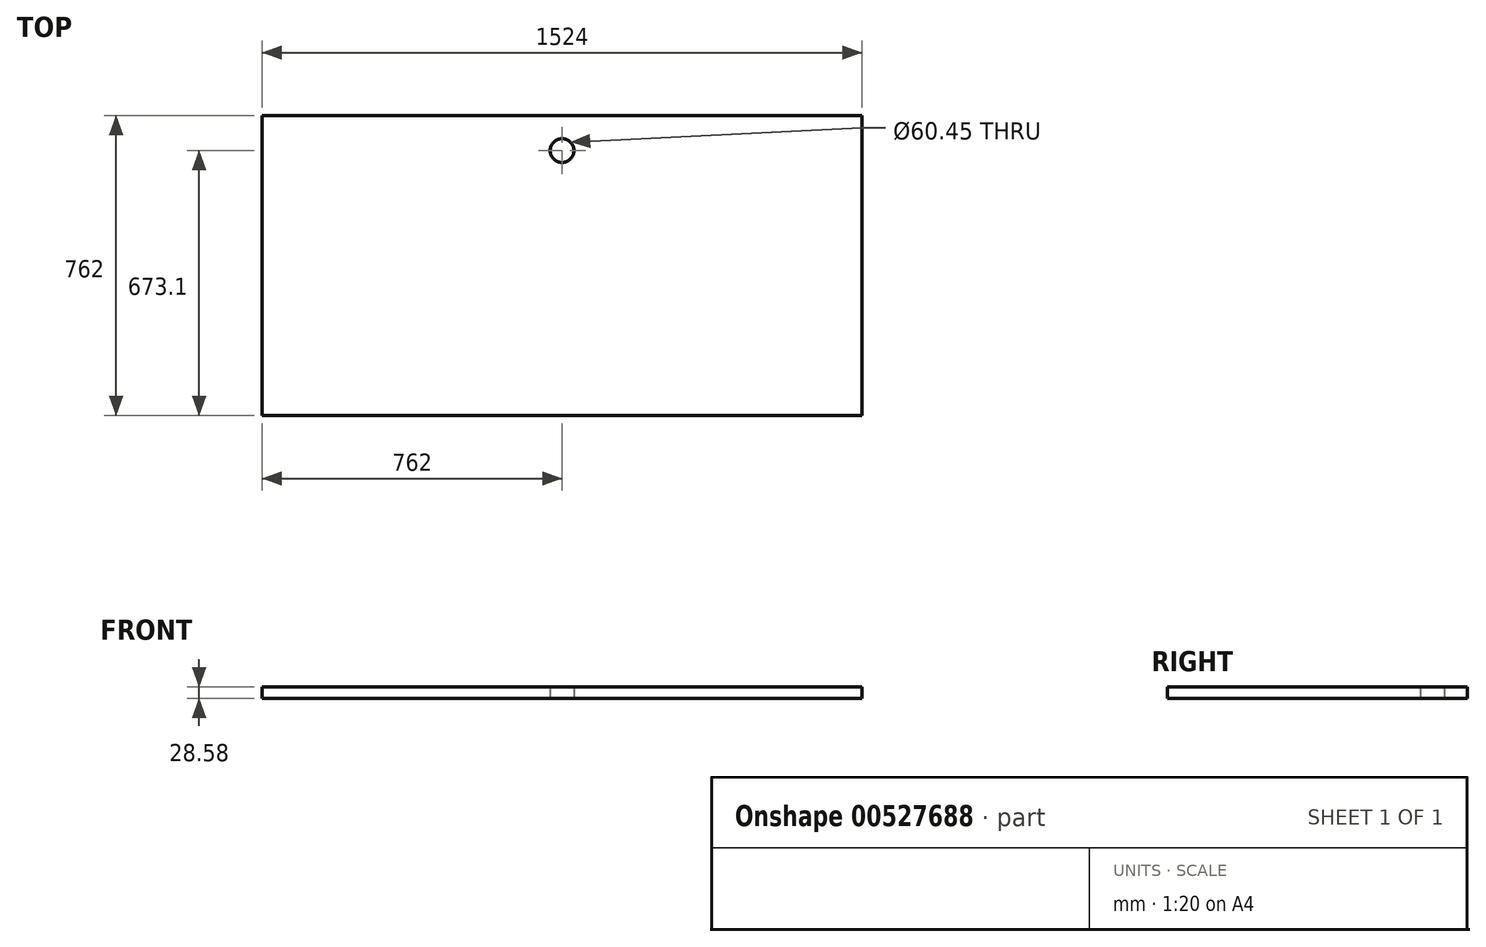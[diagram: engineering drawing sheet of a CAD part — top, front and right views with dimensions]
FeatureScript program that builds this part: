
annotation { "Feature Type Name" : "Feature", "Feature Type Description" : "" }
export const myFeature = defineFeature(function(context is Context, id is Id, definition is map)
    precondition{}
    {
        {
            var Q0;
            Q0=qCreatedBy(makeId("Top.planeOp"),FACE);
            var sketch = newSketch(context, id + "F0", { "sketchPlane" : qUnion([Q0])});
            skLineSegment(sketch, "E0.bottom", {"start": v(762, 381) * mm, "end": v(-762, 381) * mm});
            skLineSegment(sketch, "E0.top", {"start": v(762, -381) * mm, "end": v(-762, -381) * mm});
            skLineSegment(sketch, "E0.left", {"start": v(762, 381) * mm, "end": v(762, -381) * mm});
            skLineSegment(sketch, "E0.right", {"start": v(-762, 381) * mm, "end": v(-762, -381) * mm});
            skPoint(sketch, "E0.middle", {"position": v(0, 0) * mm});
            skCircle(sketch, "E1", {"center": v(0, 292.1) * mm, "radius": 30.23 * mm});
            skSolve(sketch);
        }
        {
            var Q0;
            Q0=makeQuery(id+"F0.imprint","IMPRINT",FACE,{"disambiguationData":[TD([[makeQuery(id+"F0.imprint","IMPRINT",EDGE,{"derivedFrom":sQuery(id+"F0.wireOp",EDGE,"E0.bottom")}),1.0]])]});
            extrude(context, id + "F1", {"entities" : qUnion([Q0]), "depth" : 28.57 * mm, "offsetDistance" : 25.4 * mm});
        }
    });
